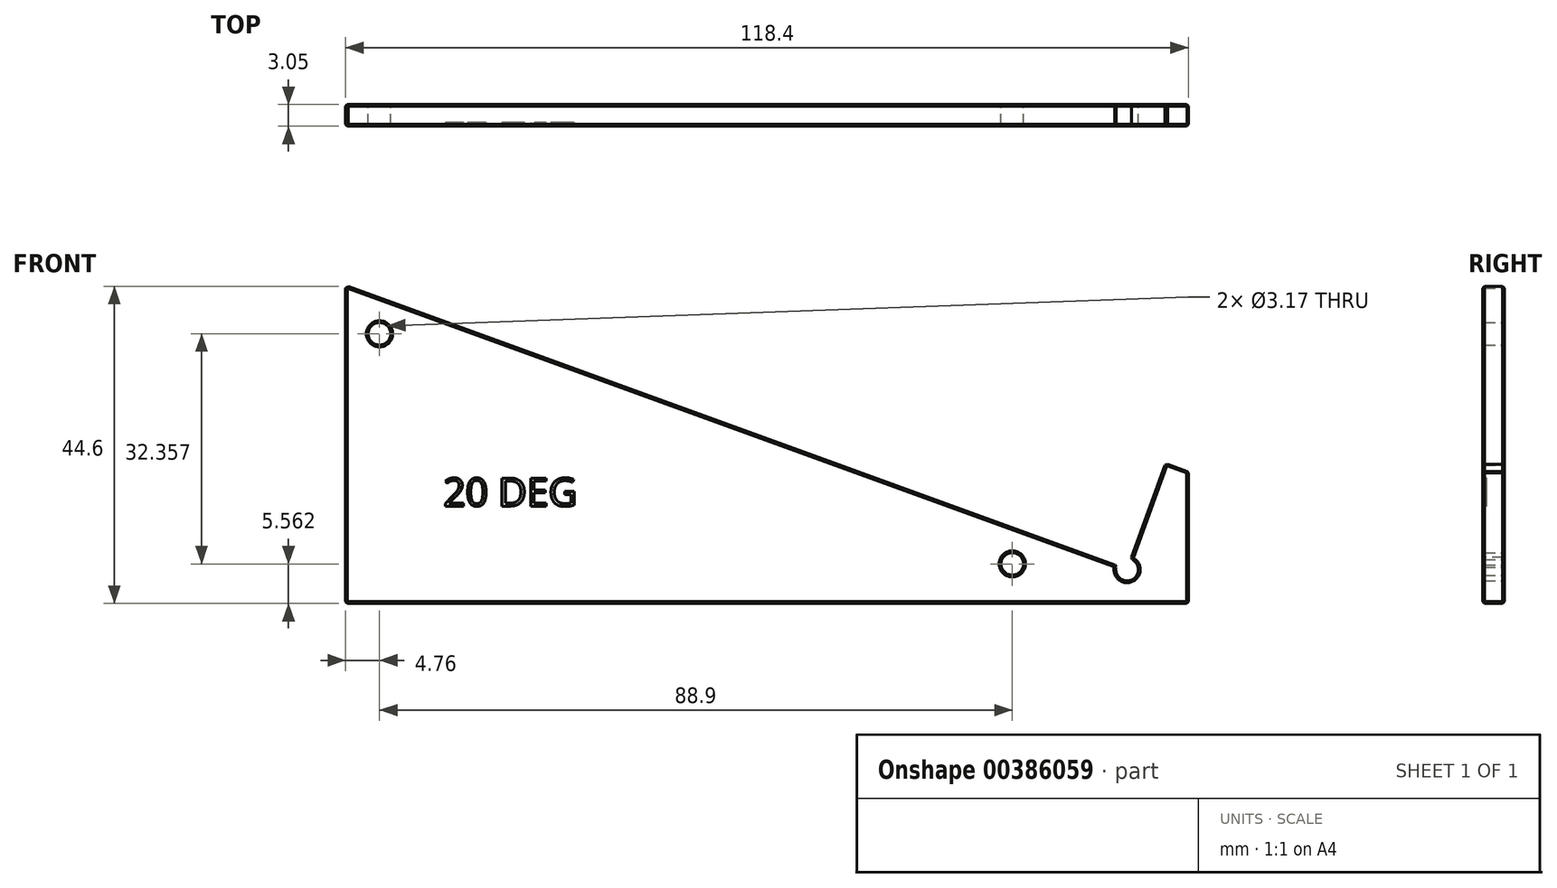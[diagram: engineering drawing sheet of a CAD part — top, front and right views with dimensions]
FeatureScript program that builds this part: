
annotation { "Feature Type Name" : "Feature", "Feature Type Description" : "" }
export const myFeature = defineFeature(function(context is Context, id is Id, definition is map)
    precondition{}
    {
        {
            var Q0;
            Q0=qCreatedBy(makeId("Front.planeOp"),FACE);
            var sketch = newSketch(context, id + "F0", { "sketchPlane" : qUnion([Q0])});
            skLineSegment(sketch, "E0", {"start": v(43.95, 2.99) * mm, "end": v(47.13, 1.83) * mm});
            skLineSegment(sketch, "E1", {"start": v(47.13, 1.83) * mm, "end": v(47.13, -16.7) * mm});
            skLineSegment(sketch, "E2", {"start": v(47.13, -16.7) * mm, "end": v(-71.27, -16.7) * mm});
            skLineSegment(sketch, "E3", {"start": v(-71.27, -16.7) * mm, "end": v(-71.27, 28.03) * mm});
            skCircle(sketch, "E4", {"center": v(-66.5, 21.23) * mm, "radius": 1.59 * mm});
            skCircle(sketch, "E5", {"center": v(22.4, -11.13) * mm, "radius": 1.59 * mm});
            skArc(sketch, "E6", {"start": v(37.03, -11.39) * mm, "mid": v(39.2, -13.37) * mm, "end": v(39.06, -10.44) * mm});
            skLineSegment(sketch, "E7", {"start": v(43.95, 2.99) * mm, "end": v(39.06, -10.44) * mm});
            skLineSegment(sketch, "E8", {"start": v(37.03, -11.39) * mm, "end": v(-71.27, 28.03) * mm});
            skLineSegment(sketch, "E9", {"start": v(-71.27, -16.7) * mm, "end": v(-71.27, 34.1) * mm});
            skLineSegment(sketch, "E10", {"start": v(-71.27, 34.1) * mm, "end": v(47.13, 34.1) * mm});
            skLineSegment(sketch, "E11", {"start": v(47.13, 34.1) * mm, "end": v(47.13, 1.83) * mm});
            skSolve(sketch);
        }
        {
            var Q0;
            Q0=makeQuery(id+"F0.imprint","IMPRINT",FACE,{"disambiguationData":[TD([[makeQuery(id+"F0.imprint","IMPRINT",EDGE,{"derivedFrom":sQuery(id+"F0.wireOp",EDGE,"E0")}),-1.0]])]});
            extrude(context, id + "F1", {"entities" : qUnion([Q0]), "depth" : 3.05 * mm, "offsetDistance" : 25.4 * mm});
        }
        {
            var Q0;
            Q0=makeQuery(id+"F1.opExtrude","CAP_FACE",FACE,{"disambiguationData":[OSD([sQuery(id+"F0.wireOp",EDGE,"E0"),sQuery(id+"F0.wireOp",EDGE,"E1"),sQuery(id+"F0.wireOp",EDGE,"E2"),sQuery(id+"F0.wireOp",EDGE,"E3"),sQuery(id+"F0.wireOp",EDGE,"E4"),sQuery(id+"F0.wireOp",EDGE,"E5"),sQuery(id+"F0.wireOp",EDGE,"E6"),sQuery(id+"F0.wireOp",EDGE,"E7"),sQuery(id+"F0.wireOp",EDGE,"E8")])],"isStart":false});
            var Q1;
            Q1=makeQuery(id+"F1.opExtrude","CAP_FACE",FACE,{"disambiguationData":[OSD([sQuery(id+"F0.wireOp",EDGE,"E0"),sQuery(id+"F0.wireOp",EDGE,"E1"),sQuery(id+"F0.wireOp",EDGE,"E2"),sQuery(id+"F0.wireOp",EDGE,"E3"),sQuery(id+"F0.wireOp",EDGE,"E4"),sQuery(id+"F0.wireOp",EDGE,"E5"),sQuery(id+"F0.wireOp",EDGE,"E6"),sQuery(id+"F0.wireOp",EDGE,"E7"),sQuery(id+"F0.wireOp",EDGE,"E8")])],"isStart":true});
            var Q2;
            Q2=makeQuery(id+"F1.opExtrude","SWEPT_EDGE",EDGE,{"disambiguationData":[OSD([sQuery(id+"F0.wireOp",EDGE,"E0"),sQuery(id+"F0.wireOp",EDGE,"E1"),sQuery(id+"F0.wireOp",EDGE,"E11")])]});
            var Q3;
            Q3=makeQuery(id+"F1.opExtrude","SWEPT_EDGE",EDGE,{"disambiguationData":[OSD([sQuery(id+"F0.wireOp",EDGE,"E0"),sQuery(id+"F0.wireOp",EDGE,"E7")])]});
            var Q4;
            Q4=makeQuery(id+"F1.opExtrude","SWEPT_EDGE",EDGE,{"disambiguationData":[OSD([sQuery(id+"F0.wireOp",EDGE,"E1"),sQuery(id+"F0.wireOp",EDGE,"E2")])]});
            var Q5;
            Q5=makeQuery(id+"F1.opExtrude","SWEPT_EDGE",EDGE,{"disambiguationData":[OSD([sQuery(id+"F0.wireOp",EDGE,"E2"),sQuery(id+"F0.wireOp",EDGE,"E3")])]});
            var Q6;
            Q6=makeQuery(id+"F1.opExtrude","SWEPT_EDGE",EDGE,{"disambiguationData":[OSD([sQuery(id+"F0.wireOp",EDGE,"E3"),sQuery(id+"F0.wireOp",EDGE,"E8"),sQuery(id+"F0.wireOp",EDGE,"E9")])]});
            var Q7;
            Q7=makeQuery(id+"F1.opExtrude","SWEPT_EDGE",EDGE,{"disambiguationData":[OSD([sQuery(id+"F0.wireOp",EDGE,"E6"),sQuery(id+"F0.wireOp",EDGE,"E8")])]});
            var Q8;
            Q8=makeQuery(id+"F1.opExtrude","SWEPT_EDGE",EDGE,{"disambiguationData":[OSD([sQuery(id+"F0.wireOp",EDGE,"E6"),sQuery(id+"F0.wireOp",EDGE,"E7")])]});
            chamfer(context, id + "F2", {"entities" : qUnion([Q0, Q1, Q2, Q3, Q4, Q5, Q6, Q7, Q8]), "width" : 0.25 * mm, "tangentPropagation" : true});
        }
        {
            var Q0;
            Q0=makeQuery(id+"F1.opExtrude","CAP_FACE",FACE,{"disambiguationData":[OSD([sQuery(id+"F0.wireOp",EDGE,"E0"),sQuery(id+"F0.wireOp",EDGE,"E1"),sQuery(id+"F0.wireOp",EDGE,"E2"),sQuery(id+"F0.wireOp",EDGE,"E3"),sQuery(id+"F0.wireOp",EDGE,"E4"),sQuery(id+"F0.wireOp",EDGE,"E5"),sQuery(id+"F0.wireOp",EDGE,"E6"),sQuery(id+"F0.wireOp",EDGE,"E7"),sQuery(id+"F0.wireOp",EDGE,"E8")])],"isStart":false});
            var sketch = newSketch(context, id + "F3", { "sketchPlane" : qUnion([Q0])});
            skText(sketch, "E12", { "text": "20 DEG", "fontName": "OpenSans-Regular.ttf"});
            const initialGuessF3  = {"E12": [-0.05755, -0.003, 1, 0, 0.00396]};
            skSetInitialGuess(sketch, initialGuessF3);
            skSolve(sketch);
        }
        {
            var Q0;
            Q0 = qSketchRegion(id + "F3", true);
            extrude(context, id + "F4", {"entities" : qUnion([Q0]), "operationType" : NewBodyOperationType.REMOVE, "oppositeDirection" : true, "depth" : 0.5 * mm, "offsetDistance" : 25.4 * mm});
        }
    });
